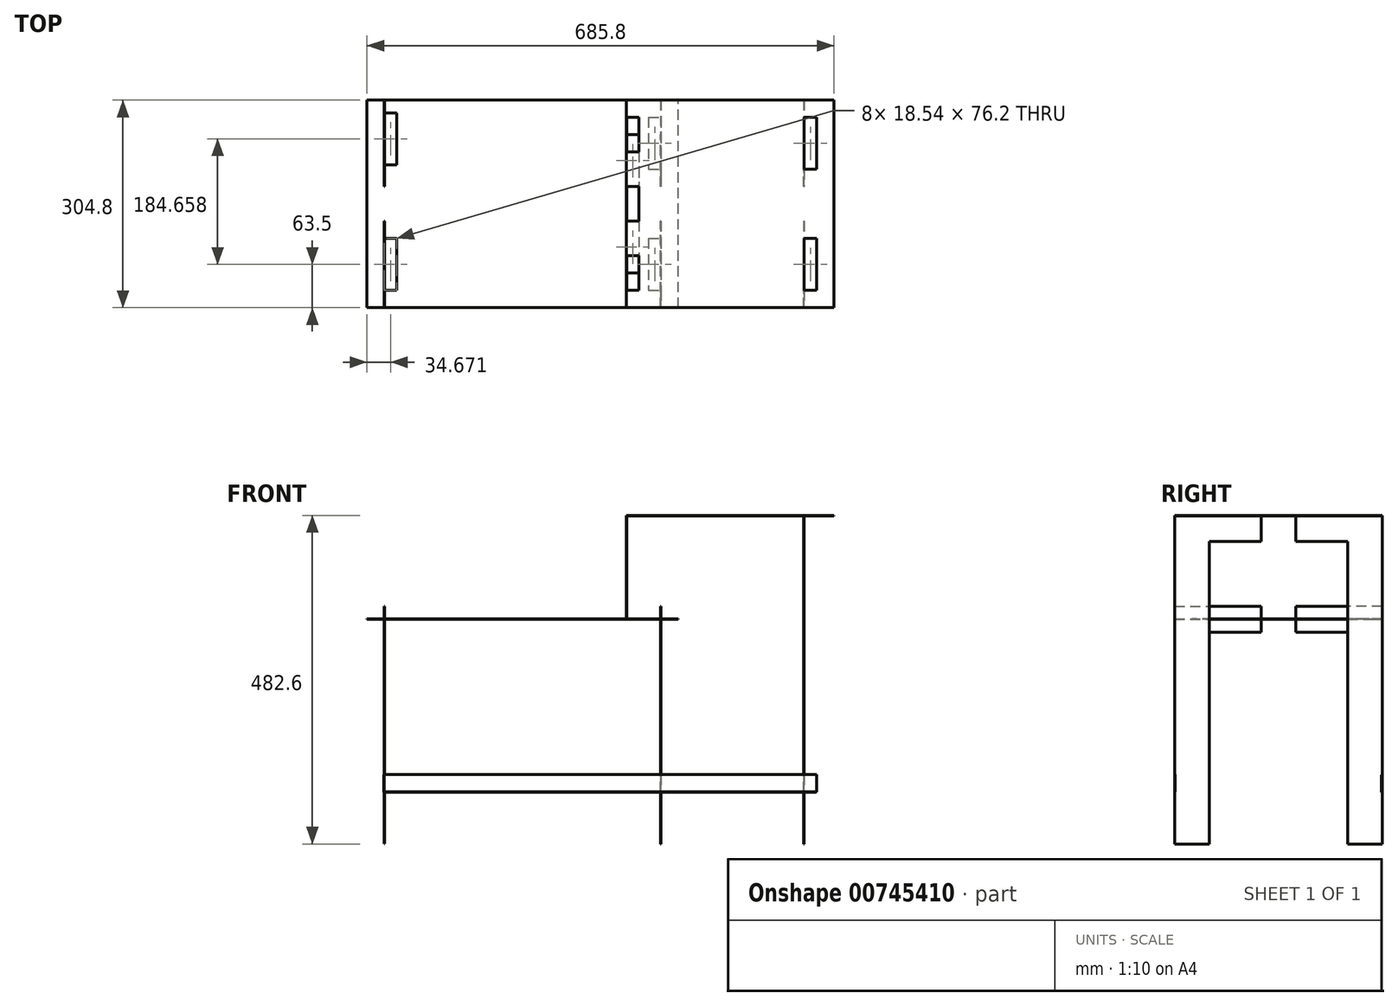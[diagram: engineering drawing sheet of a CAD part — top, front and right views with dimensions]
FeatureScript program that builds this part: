
annotation { "Feature Type Name" : "Feature", "Feature Type Description" : "" }
export const myFeature = defineFeature(function(context is Context, id is Id, definition is map)
    precondition{}
    {
        {
            assignVariable(context, id + "F0", {"name" : "ply", "anyValue" : .73});
        }
        {
            var Q0;
            Q0=qCreatedBy(makeId("Top.planeOp"),FACE);
            var sketch = newSketch(context, id + "F1", { "sketchPlane" : qUnion([Q0])});
            skLineSegment(sketch, "E0.bottom", {"start": v(0, 0) * mm, "end": v(-457.2, 0) * mm});
            skLineSegment(sketch, "E0.top", {"start": v(0, 304.8) * mm, "end": v(-457.2, 304.8) * mm});
            skLineSegment(sketch, "E0.left", {"start": v(0, 0) * mm, "end": v(0, 304.8) * mm});
            skLineSegment(sketch, "E0.right", {"start": v(-457.2, 0) * mm, "end": v(-457.2, 304.8) * mm});
            skLineSegment(sketch, "E1.bottom", {"start": v(-76.2, 254) * mm, "end": v(-57.66, 254) * mm});
            skLineSegment(sketch, "E1.top", {"start": v(-76.2, 177.8) * mm, "end": v(-57.66, 177.8) * mm});
            skLineSegment(sketch, "E1.left", {"start": v(-76.2, 254) * mm, "end": v(-76.2, 177.8) * mm});
            skLineSegment(sketch, "E1.right", {"start": v(-57.66, 254) * mm, "end": v(-57.66, 177.8) * mm});
            skLineSegment(sketch, "E2.bottom", {"start": v(-76.2, 127) * mm, "end": v(-57.66, 127) * mm});
            skLineSegment(sketch, "E2.top", {"start": v(-76.2, 50.8) * mm, "end": v(-57.66, 50.8) * mm});
            skLineSegment(sketch, "E2.left", {"start": v(-76.2, 127) * mm, "end": v(-76.2, 50.8) * mm});
            skLineSegment(sketch, "E2.right", {"start": v(-57.66, 127) * mm, "end": v(-57.66, 50.8) * mm});
            skLineSegment(sketch, "E3.bottom", {"start": v(-43.94, 279.4) * mm, "end": v(-25.4, 279.4) * mm});
            skLineSegment(sketch, "E3.top", {"start": v(-43.94, 203.2) * mm, "end": v(-25.4, 203.2) * mm});
            skLineSegment(sketch, "E3.left", {"start": v(-43.94, 279.4) * mm, "end": v(-43.94, 203.2) * mm});
            skLineSegment(sketch, "E3.right", {"start": v(-25.4, 279.4) * mm, "end": v(-25.4, 203.2) * mm});
            skLineSegment(sketch, "E4.bottom", {"start": v(-43.94, 101.6) * mm, "end": v(-25.4, 101.6) * mm});
            skLineSegment(sketch, "E4.top", {"start": v(-43.94, 25.4) * mm, "end": v(-25.4, 25.4) * mm});
            skLineSegment(sketch, "E4.left", {"start": v(-43.94, 101.6) * mm, "end": v(-43.94, 25.4) * mm});
            skLineSegment(sketch, "E4.right", {"start": v(-25.4, 101.6) * mm, "end": v(-25.4, 25.4) * mm});
            skLineSegment(sketch, "E5.bottom", {"start": v(-431.8, 101.6) * mm, "end": v(-413.26, 101.6) * mm});
            skLineSegment(sketch, "E5.top", {"start": v(-431.8, 25.4) * mm, "end": v(-413.26, 25.4) * mm});
            skLineSegment(sketch, "E5.left", {"start": v(-431.8, 101.6) * mm, "end": v(-431.8, 25.4) * mm});
            skLineSegment(sketch, "E5.right", {"start": v(-413.26, 101.6) * mm, "end": v(-413.26, 25.4) * mm});
            skLineSegment(sketch, "E6.bottom", {"start": v(-431.8, 286.26) * mm, "end": v(-413.26, 286.26) * mm});
            skLineSegment(sketch, "E6.top", {"start": v(-431.8, 210.06) * mm, "end": v(-413.26, 210.06) * mm});
            skLineSegment(sketch, "E6.left", {"start": v(-431.8, 286.26) * mm, "end": v(-431.8, 210.06) * mm});
            skLineSegment(sketch, "E6.right", {"start": v(-413.26, 286.26) * mm, "end": v(-413.26, 210.06) * mm});
            skSolve(sketch);
        }
        {
            var Q0;
            Q0=makeQuery(id+"F1.imprint","IMPRINT",FACE,{"disambiguationData":[TD([[makeQuery(id+"F1.imprint","IMPRINT",EDGE,{"derivedFrom":sQuery(id+"F1.wireOp",EDGE,"E0.bottom")}),-1.0]])]});
            var Q1;
            Q1 = qSketchRegion(id + "FDRdPOymtDaT9Mf_1", true);
            extrude(context, id + "F2", {"entities" : qUnion([Q0, Q1]), "depth" : (getVariable(context, 'ply')) * mm, "offsetDistance" : 25.4 * mm});
        }
        {
            var Q0;
            Q0=qCreatedBy(makeId("Top.planeOp"),FACE);
            cPlane(context, id + "F3", {"entities" : qUnion([Q0]), "cplaneType" : CPlaneType.OFFSET, "offset" : 152.4 * mm, "width" : 152.4 * mm, "height" : 152.4 * mm});
        }
        {
            var Q0;
            Q0=qCreatedBy(id+"F3.planeOp",FACE);
            var sketch = newSketch(context, id + "F4", { "sketchPlane" : qUnion([Q0])});
            skLineSegment(sketch, "E7.bottom", {"start": v(-76.2, 0) * mm, "end": v(228.6, 0) * mm});
            skLineSegment(sketch, "E7.top", {"start": v(-76.2, 304.8) * mm, "end": v(228.6, 304.8) * mm});
            skLineSegment(sketch, "E7.left", {"start": v(-76.2, 0) * mm, "end": v(-76.2, 25.4) * mm});
            skLineSegment(sketch, "E7.right", {"start": v(228.6, 0) * mm, "end": v(228.6, 304.8) * mm});
            skLineSegment(sketch, "E8.bottom", {"start": v(-76.2, 228.6) * mm, "end": v(-57.66, 228.6) * mm});
            skLineSegment(sketch, "E8.top", {"start": v(-76.2, 279.4) * mm, "end": v(-57.66, 279.4) * mm});
            skLineSegment(sketch, "E8.right", {"start": v(-57.66, 228.6) * mm, "end": v(-57.66, 279.4) * mm});
            skLineSegment(sketch, "E9.bottom", {"start": v(-76.2, 177.8) * mm, "end": v(-57.66, 177.8) * mm});
            skLineSegment(sketch, "E9.top", {"start": v(-76.2, 127) * mm, "end": v(-57.66, 127) * mm});
            skLineSegment(sketch, "E9.right", {"start": v(-57.66, 177.8) * mm, "end": v(-57.66, 127) * mm});
            skLineSegment(sketch, "E10.bottom", {"start": v(-76.2, 76.2) * mm, "end": v(-57.66, 76.2) * mm});
            skLineSegment(sketch, "E10.top", {"start": v(-76.2, 25.4) * mm, "end": v(-57.66, 25.4) * mm});
            skLineSegment(sketch, "E10.right", {"start": v(-57.66, 76.2) * mm, "end": v(-57.66, 25.4) * mm});
            skLineSegment(sketch, "E11.trimOffspring", {"start": v(-76.2, 279.4) * mm, "end": v(-76.2, 304.8) * mm});
            skLineSegment(sketch, "E12.trimOffspring", {"start": v(-76.2, 177.8) * mm, "end": v(-76.2, 228.6) * mm});
            skLineSegment(sketch, "E13.trimOffspring", {"start": v(-76.2, 76.2) * mm, "end": v(-76.2, 127) * mm});
            skLineSegment(sketch, "E14.bottom", {"start": v(203.2, 25.4) * mm, "end": v(184.66, 25.4) * mm});
            skLineSegment(sketch, "E14.top", {"start": v(203.2, 101.6) * mm, "end": v(184.66, 101.6) * mm});
            skLineSegment(sketch, "E14.left", {"start": v(203.2, 25.4) * mm, "end": v(203.2, 101.6) * mm});
            skLineSegment(sketch, "E14.right", {"start": v(184.66, 25.4) * mm, "end": v(184.66, 101.6) * mm});
            skLineSegment(sketch, "E15.bottom", {"start": v(184.66, 203.2) * mm, "end": v(203.2, 203.2) * mm});
            skLineSegment(sketch, "E15.top", {"start": v(184.66, 279.4) * mm, "end": v(203.2, 279.4) * mm});
            skLineSegment(sketch, "E15.left", {"start": v(184.66, 203.2) * mm, "end": v(184.66, 279.4) * mm});
            skLineSegment(sketch, "E15.right", {"start": v(203.2, 203.2) * mm, "end": v(203.2, 279.4) * mm});
            skSolve(sketch);
        }
        {
            var Q0;
            Q0 = qSketchRegion(id + "F4", true);
            extrude(context, id + "F5", {"entities" : qUnion([Q0]), "oppositeDirection" : true, "depth" : (getVariable(context, 'ply')) * mm, "offsetDistance" : 25.4 * mm});
        }
        {
            var Q0;
            Q0=makeQuery(id+"F5.opExtrude","SWEPT_FACE",FACE,{"disambiguationData":[OSD([sQuery(id+"F4.wireOp",EDGE,"E11.trimOffspring")])]});
            var sketch = newSketch(context, id + "F6", { "sketchPlane" : qUnion([Q0])});
            skLineSegment(sketch, "E16.bottom", {"start": v(-304.8, 152.4) * mm, "end": v(0, 152.4) * mm});
            skLineSegment(sketch, "E16.top", {"start": v(-304.8, 0) * mm, "end": v(0, 0) * mm});
            skLineSegment(sketch, "E16.left", {"start": v(-304.8, 152.4) * mm, "end": v(-304.8, 0) * mm});
            skLineSegment(sketch, "E16.right", {"start": v(0, 152.4) * mm, "end": v(0, 0) * mm});
            skSolve(sketch);
        }
        {
            var Q0;
            Q0 = qSketchRegion(id + "F6", true);
            extrude(context, id + "F7", {"entities" : qUnion([Q0]), "oppositeDirection" : true, "depth" : (getVariable(context, 'ply')) * mm, "offsetDistance" : 25.4 * mm});
        }
        {
            var Q0;
            Q0=makeQuery(id+"F5.opExtrude","SWEPT_BODY",BODY,{"disambiguationData":[OSD([sQuery(id+"F4.wireOp",EDGE,"E7.bottom"),sQuery(id+"F4.wireOp",EDGE,"E7.top"),sQuery(id+"F4.wireOp",EDGE,"E7.left"),sQuery(id+"F4.wireOp",EDGE,"E7.right"),sQuery(id+"F4.wireOp",EDGE,"E8.bottom"),sQuery(id+"F4.wireOp",EDGE,"E8.top"),sQuery(id+"F4.wireOp",EDGE,"E8.right"),sQuery(id+"F4.wireOp",EDGE,"E9.bottom"),sQuery(id+"F4.wireOp",EDGE,"E9.top"),sQuery(id+"F4.wireOp",EDGE,"E9.right"),sQuery(id+"F4.wireOp",EDGE,"E10.bottom"),sQuery(id+"F4.wireOp",EDGE,"E10.top"),sQuery(id+"F4.wireOp",EDGE,"E10.right"),sQuery(id+"F4.wireOp",EDGE,"E11.trimOffspring"),sQuery(id+"F4.wireOp",EDGE,"E12.trimOffspring"),sQuery(id+"F4.wireOp",EDGE,"E13.trimOffspring")])]});
            var Q1;
            Q1=makeQuery(id+"F7.opExtrude","SWEPT_BODY",BODY,{"disambiguationData":[OSD([sQuery(id+"F6.wireOp",EDGE,"E16.bottom"),sQuery(id+"F6.wireOp",EDGE,"E16.top"),sQuery(id+"F6.wireOp",EDGE,"E16.left"),sQuery(id+"F6.wireOp",EDGE,"E16.right")])]});
            booleanBodies(context, id + "F8", {"operationType" : BooleanOperationType.SUBTRACTION, "tools" : qUnion([Q0]), "targets" : qUnion([Q1]), "keepTools" : true});
        }
        {
            var Q0;
            Q0=makeQuery(id+"F5.opExtrude","SWEPT_FACE",FACE,{"disambiguationData":[OSD([sQuery(id+"F4.wireOp",EDGE,"E7.top")])]});
            cPlane(context, id + "F9", {"entities" : qUnion([Q0]), "cplaneType" : CPlaneType.OFFSET, "offset" : 152.4 * mm, "oppositeDirection" : true, "width" : 152.4 * mm, "height" : 152.4 * mm});
        }
        {
            var Q0;
            Q0=qCreatedBy(makeId("Right.planeOp"),FACE);
            var sketch = newSketch(context, id + "F10", { "sketchPlane" : qUnion([Q0])});
            skLineSegment(sketch, "E17.bottom", {"start": v(0, 152.4) * mm, "end": v(127, 152.4) * mm});
            skLineSegment(sketch, "E17.top", {"start": v(0, -330.2) * mm, "end": v(50.8, -330.2) * mm});
            skLineSegment(sketch, "E17.left", {"start": v(0, 152.4) * mm, "end": v(0, -330.2) * mm});
            skLineSegment(sketch, "E17.right", {"start": v(127, 152.4) * mm, "end": v(127, 114.3) * mm});
            skLineSegment(sketch, "E18.top", {"start": v(127, 114.3) * mm, "end": v(50.8, 114.3) * mm});
            skLineSegment(sketch, "E18.right", {"start": v(50.8, -330.2) * mm, "end": v(50.8, 114.3) * mm});
            skLineSegment(sketch, "E19.MirrorCS", {"start": v(254, -330.2) * mm, "end": v(254, 114.3) * mm});
            skLineSegment(sketch, "E20.MirrorCS", {"start": v(177.8, 114.3) * mm, "end": v(254, 114.3) * mm});
            skLineSegment(sketch, "E21.MirrorCS", {"start": v(177.8, 152.4) * mm, "end": v(177.8, 114.3) * mm});
            skLineSegment(sketch, "E22.MirrorCS", {"start": v(304.8, 152.4) * mm, "end": v(304.8, -330.2) * mm});
            skLineSegment(sketch, "E23.MirrorCS", {"start": v(304.8, 152.4) * mm, "end": v(177.8, 152.4) * mm});
            skLineSegment(sketch, "E24.MirrorCS", {"start": v(304.8, -330.2) * mm, "end": v(254, -330.2) * mm});
            skSolve(sketch);
        }
        {
            var Q0;
            Q0 = qSketchRegion(id + "F10", true);
            extrude(context, id + "F11", {"entities" : qUnion([Q0]), "depth" : (getVariable(context, 'ply')) * mm, "offsetDistance" : 25.4 * mm});
        }
        {
            var Q0;
            Q0=makeQuery(id+"F11.opExtrude","SWEPT_BODY",BODY,{"disambiguationData":[OSD([sQuery(id+"F10.wireOp",EDGE,"E17.bottom"),sQuery(id+"F10.wireOp",EDGE,"E17.top"),sQuery(id+"F10.wireOp",EDGE,"E17.left"),sQuery(id+"F10.wireOp",EDGE,"E17.right"),sQuery(id+"F10.wireOp",EDGE,"E18.top"),sQuery(id+"F10.wireOp",EDGE,"E18.right")])]});
            var Q1;
            Q1=makeQuery(id+"F5.opExtrude","SWEPT_FACE",FACE,{"disambiguationData":[OSD([sQuery(id+"F4.wireOp",EDGE,"E14.right")])]});
            transform(context, id + "F12", {"entities" : qUnion([Q0]), "transformType" : TransformType.TRANSLATION_DISTANCE, "transformDirection" : qUnion([Q1]), "distance" : 184.15 * mm, "makeCopy" : false});
        }
        {
            var Q0;
            Q0=makeQuery(id+"F5.opExtrude","SWEPT_BODY",BODY,{"disambiguationData":[OSD([sQuery(id+"F4.wireOp",EDGE,"E7.bottom"),sQuery(id+"F4.wireOp",EDGE,"E7.top"),sQuery(id+"F4.wireOp",EDGE,"E7.left"),sQuery(id+"F4.wireOp",EDGE,"E7.right"),sQuery(id+"F4.wireOp",EDGE,"E8.bottom"),sQuery(id+"F4.wireOp",EDGE,"E8.top"),sQuery(id+"F4.wireOp",EDGE,"E8.right"),sQuery(id+"F4.wireOp",EDGE,"E9.bottom"),sQuery(id+"F4.wireOp",EDGE,"E9.top"),sQuery(id+"F4.wireOp",EDGE,"E9.right"),sQuery(id+"F4.wireOp",EDGE,"E10.bottom"),sQuery(id+"F4.wireOp",EDGE,"E10.top"),sQuery(id+"F4.wireOp",EDGE,"E10.right"),sQuery(id+"F4.wireOp",EDGE,"E11.trimOffspring"),sQuery(id+"F4.wireOp",EDGE,"E12.trimOffspring"),sQuery(id+"F4.wireOp",EDGE,"E13.trimOffspring"),sQuery(id+"F4.wireOp",EDGE,"E14.bottom"),sQuery(id+"F4.wireOp",EDGE,"E14.top"),sQuery(id+"F4.wireOp",EDGE,"E14.left"),sQuery(id+"F4.wireOp",EDGE,"E14.right"),sQuery(id+"F4.wireOp",EDGE,"E15.bottom"),sQuery(id+"F4.wireOp",EDGE,"E15.top"),sQuery(id+"F4.wireOp",EDGE,"E15.left"),sQuery(id+"F4.wireOp",EDGE,"E15.right")])]});
            var Q1;
            Q1=makeQuery(id+"F11.opExtrude","SWEPT_BODY",BODY,{"disambiguationData":[OSD([sQuery(id+"F10.wireOp",EDGE,"E17.bottom"),sQuery(id+"F10.wireOp",EDGE,"E17.top"),sQuery(id+"F10.wireOp",EDGE,"E17.left"),sQuery(id+"F10.wireOp",EDGE,"E17.right"),sQuery(id+"F10.wireOp",EDGE,"E18.top"),sQuery(id+"F10.wireOp",EDGE,"E18.right")])]});
            booleanBodies(context, id + "F13", {"operationType" : BooleanOperationType.SUBTRACTION, "tools" : qUnion([Q0]), "targets" : qUnion([Q1]), "keepTools" : true});
        }
        {
            var Q0;
            Q0=makeQuery(id+"F11.opExtrude","SWEPT_BODY",BODY,{"disambiguationData":[OSD([sQuery(id+"F10.wireOp",EDGE,"E19.MirrorCS"),sQuery(id+"F10.wireOp",EDGE,"E20.MirrorCS"),sQuery(id+"F10.wireOp",EDGE,"E21.MirrorCS"),sQuery(id+"F10.wireOp",EDGE,"E22.MirrorCS"),sQuery(id+"F10.wireOp",EDGE,"E23.MirrorCS"),sQuery(id+"F10.wireOp",EDGE,"E24.MirrorCS")])]});
            var Q1;
            Q1=makeQuery(id+"F5.opExtrude","SWEPT_FACE",FACE,{"disambiguationData":[OSD([sQuery(id+"F4.wireOp",EDGE,"E15.left")])]});
            transform(context, id + "F14", {"entities" : qUnion([Q0]), "transformType" : TransformType.TRANSLATION_DISTANCE, "transformDirection" : qUnion([Q1]), "distance" : 184.15 * mm, "makeCopy" : false});
        }
        {
            var Q0;
            Q0=makeQuery(id+"F5.opExtrude","SWEPT_BODY",BODY,{"disambiguationData":[OSD([sQuery(id+"F4.wireOp",EDGE,"E7.bottom"),sQuery(id+"F4.wireOp",EDGE,"E7.top"),sQuery(id+"F4.wireOp",EDGE,"E7.left"),sQuery(id+"F4.wireOp",EDGE,"E7.right"),sQuery(id+"F4.wireOp",EDGE,"E8.bottom"),sQuery(id+"F4.wireOp",EDGE,"E8.top"),sQuery(id+"F4.wireOp",EDGE,"E8.right"),sQuery(id+"F4.wireOp",EDGE,"E9.bottom"),sQuery(id+"F4.wireOp",EDGE,"E9.top"),sQuery(id+"F4.wireOp",EDGE,"E9.right"),sQuery(id+"F4.wireOp",EDGE,"E10.bottom"),sQuery(id+"F4.wireOp",EDGE,"E10.top"),sQuery(id+"F4.wireOp",EDGE,"E10.right"),sQuery(id+"F4.wireOp",EDGE,"E11.trimOffspring"),sQuery(id+"F4.wireOp",EDGE,"E12.trimOffspring"),sQuery(id+"F4.wireOp",EDGE,"E13.trimOffspring"),sQuery(id+"F4.wireOp",EDGE,"E14.bottom"),sQuery(id+"F4.wireOp",EDGE,"E14.top"),sQuery(id+"F4.wireOp",EDGE,"E14.left"),sQuery(id+"F4.wireOp",EDGE,"E14.right"),sQuery(id+"F4.wireOp",EDGE,"E15.bottom"),sQuery(id+"F4.wireOp",EDGE,"E15.top"),sQuery(id+"F4.wireOp",EDGE,"E15.left"),sQuery(id+"F4.wireOp",EDGE,"E15.right")])]});
            var Q1;
            Q1=makeQuery(id+"F11.opExtrude","SWEPT_BODY",BODY,{"disambiguationData":[OSD([sQuery(id+"F10.wireOp",EDGE,"E19.MirrorCS"),sQuery(id+"F10.wireOp",EDGE,"E20.MirrorCS"),sQuery(id+"F10.wireOp",EDGE,"E21.MirrorCS"),sQuery(id+"F10.wireOp",EDGE,"E22.MirrorCS"),sQuery(id+"F10.wireOp",EDGE,"E23.MirrorCS"),sQuery(id+"F10.wireOp",EDGE,"E24.MirrorCS")])]});
            booleanBodies(context, id + "F15", {"operationType" : BooleanOperationType.SUBTRACTION, "tools" : qUnion([Q0]), "targets" : qUnion([Q1]), "keepTools" : true});
        }
        {
            var Q0;
            Q0=makeQuery(id+"F2.opExtrude","SWEPT_BODY",BODY,{"disambiguationData":[OSD([sQuery(id+"F1.wireOp",EDGE,"E0.bottom"),sQuery(id+"F1.wireOp",EDGE,"E0.top"),sQuery(id+"F1.wireOp",EDGE,"E0.left"),sQuery(id+"F1.wireOp",EDGE,"E0.right"),sQuery(id+"F1.wireOp",EDGE,"E1.bottom"),sQuery(id+"F1.wireOp",EDGE,"E1.top"),sQuery(id+"F1.wireOp",EDGE,"E1.left"),sQuery(id+"F1.wireOp",EDGE,"E1.right"),sQuery(id+"F1.wireOp",EDGE,"E2.bottom"),sQuery(id+"F1.wireOp",EDGE,"E2.top"),sQuery(id+"F1.wireOp",EDGE,"E2.left"),sQuery(id+"F1.wireOp",EDGE,"E2.right")])]});
            var Q1;
            Q1=makeQuery(id+"F7.opExtrude","SWEPT_BODY",BODY,{"disambiguationData":[OSD([sQuery(id+"F6.wireOp",EDGE,"E16.bottom"),sQuery(id+"F6.wireOp",EDGE,"E16.top"),sQuery(id+"F6.wireOp",EDGE,"E16.left"),sQuery(id+"F6.wireOp",EDGE,"E16.right")])]});
            booleanBodies(context, id + "F16", {"operationType" : BooleanOperationType.SUBTRACTION, "tools" : qUnion([Q0]), "targets" : qUnion([Q1]), "keepTools" : true});
        }
        {
            var Q0;
            Q0=qCreatedBy(makeId("Right.planeOp"),FACE);
            var sketch = newSketch(context, id + "F17", { "sketchPlane" : qUnion([Q0])});
            skLineSegment(sketch, "E25.bottom", {"start": v(0, 18.54) * mm, "end": v(127, 18.54) * mm});
            skLineSegment(sketch, "E25.top", {"start": v(0, -330.2) * mm, "end": v(50.8, -330.2) * mm});
            skLineSegment(sketch, "E25.left", {"start": v(0, 18.54) * mm, "end": v(0, -330.2) * mm});
            skLineSegment(sketch, "E25.right", {"start": v(127, 18.54) * mm, "end": v(127, -19.56) * mm});
            skLineSegment(sketch, "E26.top", {"start": v(127, -19.56) * mm, "end": v(50.8, -19.56) * mm});
            skLineSegment(sketch, "E26.right", {"start": v(50.8, -330.2) * mm, "end": v(50.8, -19.56) * mm});
            skLineSegment(sketch, "E27.MirrorCS", {"start": v(177.8, 18.54) * mm, "end": v(177.8, -19.56) * mm});
            skLineSegment(sketch, "E28.MirrorCS", {"start": v(254, -330.2) * mm, "end": v(254, -19.56) * mm});
            skLineSegment(sketch, "E29.MirrorCS", {"start": v(177.8, -19.56) * mm, "end": v(254, -19.56) * mm});
            skLineSegment(sketch, "E30.MirrorCS", {"start": v(304.8, 18.54) * mm, "end": v(304.8, -330.2) * mm});
            skLineSegment(sketch, "E31.MirrorCS", {"start": v(304.8, -330.2) * mm, "end": v(254, -330.2) * mm});
            skLineSegment(sketch, "E32.MirrorCS", {"start": v(304.8, 18.54) * mm, "end": v(177.8, 18.54) * mm});
            skSolve(sketch);
        }
        {
            var Q0;
            Q0 = qSketchRegion(id + "F17", true);
            extrude(context, id + "F18", {"entities" : qUnion([Q0]), "oppositeDirection" : true, "depth" : (getVariable(context, 'ply')) * mm, "offsetDistance" : 25.4 * mm});
        }
        {
            var Q0;
            Q0=makeQuery(id+"F18.opExtrude","SWEPT_BODY",BODY,{"disambiguationData":[OSD([sQuery(id+"F17.wireOp",EDGE,"E25.bottom"),sQuery(id+"F17.wireOp",EDGE,"E25.top"),sQuery(id+"F17.wireOp",EDGE,"E25.left"),sQuery(id+"F17.wireOp",EDGE,"E25.right"),sQuery(id+"F17.wireOp",EDGE,"E26.top"),sQuery(id+"F17.wireOp",EDGE,"E26.right")])]});
            var Q1;
            Q1=makeQuery(id+"F2.opExtrude","SWEPT_FACE",FACE,{"disambiguationData":[OSD([sQuery(id+"F1.wireOp",EDGE,"E0.right")])]});
            transform(context, id + "F19", {"entities" : qUnion([Q0]), "transformType" : TransformType.TRANSLATION_DISTANCE, "transformDirection" : qUnion([Q1]), "distance" : 25.4 * mm, "makeCopy" : false});
        }
        {
            var Q0;
            Q0=makeQuery(id+"F2.opExtrude","SWEPT_BODY",BODY,{"disambiguationData":[OSD([sQuery(id+"F1.wireOp",EDGE,"E0.bottom"),sQuery(id+"F1.wireOp",EDGE,"E0.top"),sQuery(id+"F1.wireOp",EDGE,"E0.left"),sQuery(id+"F1.wireOp",EDGE,"E0.right"),sQuery(id+"F1.wireOp",EDGE,"E1.bottom"),sQuery(id+"F1.wireOp",EDGE,"E1.top"),sQuery(id+"F1.wireOp",EDGE,"E1.left"),sQuery(id+"F1.wireOp",EDGE,"E1.right"),sQuery(id+"F1.wireOp",EDGE,"E2.bottom"),sQuery(id+"F1.wireOp",EDGE,"E2.top"),sQuery(id+"F1.wireOp",EDGE,"E2.left"),sQuery(id+"F1.wireOp",EDGE,"E2.right"),sQuery(id+"F1.wireOp",EDGE,"E3.bottom"),sQuery(id+"F1.wireOp",EDGE,"E3.top"),sQuery(id+"F1.wireOp",EDGE,"E3.left"),sQuery(id+"F1.wireOp",EDGE,"E3.right"),sQuery(id+"F1.wireOp",EDGE,"E4.bottom"),sQuery(id+"F1.wireOp",EDGE,"E4.top"),sQuery(id+"F1.wireOp",EDGE,"E4.left"),sQuery(id+"F1.wireOp",EDGE,"E4.right")])]});
            var Q1;
            Q1=makeQuery(id+"F18.opExtrude","SWEPT_BODY",BODY,{"disambiguationData":[OSD([sQuery(id+"F17.wireOp",EDGE,"E25.bottom"),sQuery(id+"F17.wireOp",EDGE,"E25.top"),sQuery(id+"F17.wireOp",EDGE,"E25.left"),sQuery(id+"F17.wireOp",EDGE,"E25.right"),sQuery(id+"F17.wireOp",EDGE,"E26.top"),sQuery(id+"F17.wireOp",EDGE,"E26.right")])]});
            booleanBodies(context, id + "F20", {"operationType" : BooleanOperationType.SUBTRACTION, "tools" : qUnion([Q0]), "targets" : qUnion([Q1]), "keepTools" : true});
        }
        {
            var Q0;
            Q0=makeQuery(id+"F18.opExtrude","SWEPT_BODY",BODY,{"disambiguationData":[OSD([sQuery(id+"F17.wireOp",EDGE,"E27.MirrorCS"),sQuery(id+"F17.wireOp",EDGE,"E28.MirrorCS"),sQuery(id+"F17.wireOp",EDGE,"E29.MirrorCS"),sQuery(id+"F17.wireOp",EDGE,"E30.MirrorCS"),sQuery(id+"F17.wireOp",EDGE,"E31.MirrorCS"),sQuery(id+"F17.wireOp",EDGE,"E32.MirrorCS")])]});
            var Q1;
            Q1=makeQuery(id+"F2.opExtrude","SWEPT_FACE",FACE,{"disambiguationData":[OSD([sQuery(id+"F1.wireOp",EDGE,"E0.right")])]});
            transform(context, id + "F21", {"entities" : qUnion([Q0]), "transformType" : TransformType.TRANSLATION_DISTANCE, "transformDirection" : qUnion([Q1]), "distance" : 25.4 * mm, "makeCopy" : false});
        }
        {
            var Q0;
            Q0=makeQuery(id+"F2.opExtrude","SWEPT_BODY",BODY,{"disambiguationData":[OSD([sQuery(id+"F1.wireOp",EDGE,"E0.bottom"),sQuery(id+"F1.wireOp",EDGE,"E0.top"),sQuery(id+"F1.wireOp",EDGE,"E0.left"),sQuery(id+"F1.wireOp",EDGE,"E0.right"),sQuery(id+"F1.wireOp",EDGE,"E1.bottom"),sQuery(id+"F1.wireOp",EDGE,"E1.top"),sQuery(id+"F1.wireOp",EDGE,"E1.left"),sQuery(id+"F1.wireOp",EDGE,"E1.right"),sQuery(id+"F1.wireOp",EDGE,"E2.bottom"),sQuery(id+"F1.wireOp",EDGE,"E2.top"),sQuery(id+"F1.wireOp",EDGE,"E2.left"),sQuery(id+"F1.wireOp",EDGE,"E2.right"),sQuery(id+"F1.wireOp",EDGE,"E3.bottom"),sQuery(id+"F1.wireOp",EDGE,"E3.top"),sQuery(id+"F1.wireOp",EDGE,"E3.left"),sQuery(id+"F1.wireOp",EDGE,"E3.right"),sQuery(id+"F1.wireOp",EDGE,"E4.bottom"),sQuery(id+"F1.wireOp",EDGE,"E4.top"),sQuery(id+"F1.wireOp",EDGE,"E4.left"),sQuery(id+"F1.wireOp",EDGE,"E4.right")])]});
            var Q1;
            Q1=makeQuery(id+"F18.opExtrude","SWEPT_BODY",BODY,{"disambiguationData":[OSD([sQuery(id+"F17.wireOp",EDGE,"E27.MirrorCS"),sQuery(id+"F17.wireOp",EDGE,"E28.MirrorCS"),sQuery(id+"F17.wireOp",EDGE,"E29.MirrorCS"),sQuery(id+"F17.wireOp",EDGE,"E30.MirrorCS"),sQuery(id+"F17.wireOp",EDGE,"E31.MirrorCS"),sQuery(id+"F17.wireOp",EDGE,"E32.MirrorCS")])]});
            booleanBodies(context, id + "F22", {"operationType" : BooleanOperationType.SUBTRACTION, "tools" : qUnion([Q0]), "targets" : qUnion([Q1]), "keepTools" : true});
        }
        {
            var Q0;
            Q0=makeQuery(id+"F2.opExtrude","SWEPT_FACE",FACE,{"disambiguationData":[OSD([sQuery(id+"F1.wireOp",EDGE,"E0.right")])]});
            var sketch = newSketch(context, id + "F23", { "sketchPlane" : qUnion([Q0])});
            skLineSegment(sketch, "E33.bottom", {"start": v(-304.8, 18.54) * mm, "end": v(-177.8, 18.54) * mm});
            skLineSegment(sketch, "E33.top", {"start": v(-304.8, -329.95) * mm, "end": v(-254, -329.95) * mm});
            skLineSegment(sketch, "E33.left", {"start": v(-304.8, 18.54) * mm, "end": v(-304.8, -329.95) * mm});
            skLineSegment(sketch, "E33.right", {"start": v(-177.8, 18.54) * mm, "end": v(-177.8, -18.8) * mm});
            skLineSegment(sketch, "E34.top", {"start": v(-177.8, -18.8) * mm, "end": v(-254, -18.8) * mm});
            skLineSegment(sketch, "E34.right", {"start": v(-254, -329.95) * mm, "end": v(-254, -18.8) * mm});
            skLineSegment(sketch, "E35.MirrorCS", {"start": v(-50.8, -329.95) * mm, "end": v(-50.8, -18.8) * mm});
            skLineSegment(sketch, "E36.MirrorCS", {"start": v(-127, -18.8) * mm, "end": v(-50.8, -18.8) * mm});
            skLineSegment(sketch, "E37.MirrorCS", {"start": v(-127, 18.54) * mm, "end": v(-127, -18.8) * mm});
            skLineSegment(sketch, "E38.MirrorCS", {"start": v(0, 18.54) * mm, "end": v(0, -329.95) * mm});
            skLineSegment(sketch, "E39.MirrorCS", {"start": v(0, -329.95) * mm, "end": v(-50.8, -329.95) * mm});
            skLineSegment(sketch, "E40.MirrorCS", {"start": v(0, 18.54) * mm, "end": v(-127, 18.54) * mm});
            skSolve(sketch);
        }
        {
            var Q0;
            Q0 = qSketchRegion(id + "F23", true);
            extrude(context, id + "F24", {"entities" : qUnion([Q0]), "oppositeDirection" : true, "depth" : (getVariable(context, 'ply')) * mm, "offsetDistance" : 25.4 * mm});
        }
        {
            var Q0;
            Q0=makeQuery(id+"F24.opExtrude","SWEPT_BODY",BODY,{"disambiguationData":[OSD([sQuery(id+"F23.wireOp",EDGE,"E33.bottom"),sQuery(id+"F23.wireOp",EDGE,"E33.top"),sQuery(id+"F23.wireOp",EDGE,"E33.left"),sQuery(id+"F23.wireOp",EDGE,"E33.right"),sQuery(id+"F23.wireOp",EDGE,"E34.top"),sQuery(id+"F23.wireOp",EDGE,"E34.right")])]});
            var Q1;
            Q1=makeQuery(id+"F24.opExtrude","SWEPT_BODY",BODY,{"disambiguationData":[OSD([sQuery(id+"F23.wireOp",EDGE,"E35.MirrorCS"),sQuery(id+"F23.wireOp",EDGE,"E36.MirrorCS"),sQuery(id+"F23.wireOp",EDGE,"E37.MirrorCS"),sQuery(id+"F23.wireOp",EDGE,"E38.MirrorCS"),sQuery(id+"F23.wireOp",EDGE,"E39.MirrorCS"),sQuery(id+"F23.wireOp",EDGE,"E40.MirrorCS")])]});
            var Q2;
            Q2=makeQuery(id+"F2.opExtrude","SWEPT_FACE",FACE,{"disambiguationData":[OSD([sQuery(id+"F1.wireOp",EDGE,"E0.right")])]});
            transform(context, id + "F25", {"entities" : qUnion([Q0, Q1]), "transformType" : TransformType.TRANSLATION_DISTANCE, "transformDirection" : qUnion([Q2]), "distance" : 25.4 * mm, "oppositeDirection" : true, "makeCopy" : false});
        }
        {
            var Q0;
            Q0=makeQuery(id+"F2.opExtrude","SWEPT_BODY",BODY,{"disambiguationData":[OSD([sQuery(id+"F1.wireOp",EDGE,"E0.bottom"),sQuery(id+"F1.wireOp",EDGE,"E0.top"),sQuery(id+"F1.wireOp",EDGE,"E0.left"),sQuery(id+"F1.wireOp",EDGE,"E0.right"),sQuery(id+"F1.wireOp",EDGE,"E1.bottom"),sQuery(id+"F1.wireOp",EDGE,"E1.top"),sQuery(id+"F1.wireOp",EDGE,"E1.left"),sQuery(id+"F1.wireOp",EDGE,"E1.right"),sQuery(id+"F1.wireOp",EDGE,"E2.bottom"),sQuery(id+"F1.wireOp",EDGE,"E2.top"),sQuery(id+"F1.wireOp",EDGE,"E2.left"),sQuery(id+"F1.wireOp",EDGE,"E2.right"),sQuery(id+"F1.wireOp",EDGE,"E3.bottom"),sQuery(id+"F1.wireOp",EDGE,"E3.top"),sQuery(id+"F1.wireOp",EDGE,"E3.left"),sQuery(id+"F1.wireOp",EDGE,"E3.right"),sQuery(id+"F1.wireOp",EDGE,"E4.bottom"),sQuery(id+"F1.wireOp",EDGE,"E4.top"),sQuery(id+"F1.wireOp",EDGE,"E4.left"),sQuery(id+"F1.wireOp",EDGE,"E4.right"),sQuery(id+"F1.wireOp",EDGE,"E5.bottom"),sQuery(id+"F1.wireOp",EDGE,"E5.top"),sQuery(id+"F1.wireOp",EDGE,"E5.left"),sQuery(id+"F1.wireOp",EDGE,"E5.right"),sQuery(id+"F1.wireOp",EDGE,"E6.bottom"),sQuery(id+"F1.wireOp",EDGE,"E6.top"),sQuery(id+"F1.wireOp",EDGE,"E6.left"),sQuery(id+"F1.wireOp",EDGE,"E6.right")])]});
            var Q1;
            Q1=makeQuery(id+"F24.opExtrude","SWEPT_BODY",BODY,{"disambiguationData":[OSD([sQuery(id+"F23.wireOp",EDGE,"E35.MirrorCS"),sQuery(id+"F23.wireOp",EDGE,"E36.MirrorCS"),sQuery(id+"F23.wireOp",EDGE,"E37.MirrorCS"),sQuery(id+"F23.wireOp",EDGE,"E38.MirrorCS"),sQuery(id+"F23.wireOp",EDGE,"E39.MirrorCS"),sQuery(id+"F23.wireOp",EDGE,"E40.MirrorCS")])]});
            var Q2;
            Q2=makeQuery(id+"F24.opExtrude","SWEPT_BODY",BODY,{"disambiguationData":[OSD([sQuery(id+"F23.wireOp",EDGE,"E33.bottom"),sQuery(id+"F23.wireOp",EDGE,"E33.top"),sQuery(id+"F23.wireOp",EDGE,"E33.left"),sQuery(id+"F23.wireOp",EDGE,"E33.right"),sQuery(id+"F23.wireOp",EDGE,"E34.top"),sQuery(id+"F23.wireOp",EDGE,"E34.right")])]});
            booleanBodies(context, id + "F26", {"operationType" : BooleanOperationType.SUBTRACTION, "tools" : qUnion([Q0]), "targets" : qUnion([Q1, Q2]), "keepTools" : true});
        }
        {
            var Q0;
            Q0=makeQuery(id+"F24.opExtrude","SWEPT_FACE",FACE,{"disambiguationData":[OSD([sQuery(id+"F23.wireOp",EDGE,"E38.MirrorCS")])]});
            var sketch = newSketch(context, id + "F27", { "sketchPlane" : qUnion([Q0])});
            skLineSegment(sketch, "E41.bottom", {"start": v(-431.8, -253.75) * mm, "end": v(203.2, -253.75) * mm});
            skLineSegment(sketch, "E41.top", {"start": v(-431.8, -228.35) * mm, "end": v(203.2, -228.35) * mm});
            skLineSegment(sketch, "E41.left", {"start": v(-431.8, -253.75) * mm, "end": v(-431.8, -228.35) * mm});
            skLineSegment(sketch, "E41.right", {"start": v(203.2, -253.75) * mm, "end": v(203.2, -228.35) * mm});
            skSolve(sketch);
        }
        {
            var Q0;
            Q0 = qSketchRegion(id + "F27", true);
            extrude(context, id + "F28", {"entities" : qUnion([Q0]), "oppositeDirection" : true, "depth" : (getVariable(context, 'ply')) * mm, "offsetDistance" : 25.4 * mm});
        }
        {
            var Q0;
            Q0=makeQuery(id+"F11.opExtrude","SWEPT_FACE",FACE,{"disambiguationData":[OSD([sQuery(id+"F10.wireOp",EDGE,"E22.MirrorCS")])]});
            var sketch = newSketch(context, id + "F29", { "sketchPlane" : qUnion([Q0])});
            skLineSegment(sketch, "E42.bottom", {"start": v(-202.7, -228.6) * mm, "end": v(432.3, -228.6) * mm});
            skLineSegment(sketch, "E42.top", {"start": v(-202.7, -254) * mm, "end": v(432.3, -254) * mm});
            skLineSegment(sketch, "E42.left", {"start": v(-202.7, -228.6) * mm, "end": v(-202.7, -254) * mm});
            skLineSegment(sketch, "E42.right", {"start": v(432.3, -228.6) * mm, "end": v(432.3, -254) * mm});
            skSolve(sketch);
        }
        {
            var Q0;
            Q0 = qSketchRegion(id + "F29", true);
            extrude(context, id + "F30", {"entities" : qUnion([Q0]), "oppositeDirection" : true, "depth" : (getVariable(context, 'ply')) * mm, "offsetDistance" : 25.4 * mm});
        }
        {
            var Q0;
            Q0=makeQuery(id+"F28.opExtrude","SWEPT_BODY",BODY,{"disambiguationData":[OSD([sQuery(id+"F27.wireOp",EDGE,"E41.bottom"),sQuery(id+"F27.wireOp",EDGE,"E41.top"),sQuery(id+"F27.wireOp",EDGE,"E41.left"),sQuery(id+"F27.wireOp",EDGE,"E41.right")])]});
            var Q1;
            Q1=makeQuery(id+"F24.opExtrude","SWEPT_BODY",BODY,{"disambiguationData":[OSD([sQuery(id+"F23.wireOp",EDGE,"E35.MirrorCS"),sQuery(id+"F23.wireOp",EDGE,"E36.MirrorCS"),sQuery(id+"F23.wireOp",EDGE,"E37.MirrorCS"),sQuery(id+"F23.wireOp",EDGE,"E38.MirrorCS"),sQuery(id+"F23.wireOp",EDGE,"E39.MirrorCS"),sQuery(id+"F23.wireOp",EDGE,"E40.MirrorCS")])]});
            var Q2;
            Q2=makeQuery(id+"F18.opExtrude","SWEPT_BODY",BODY,{"disambiguationData":[OSD([sQuery(id+"F17.wireOp",EDGE,"E25.bottom"),sQuery(id+"F17.wireOp",EDGE,"E25.top"),sQuery(id+"F17.wireOp",EDGE,"E25.left"),sQuery(id+"F17.wireOp",EDGE,"E25.right"),sQuery(id+"F17.wireOp",EDGE,"E26.top"),sQuery(id+"F17.wireOp",EDGE,"E26.right")])]});
            var Q3;
            Q3=makeQuery(id+"F11.opExtrude","SWEPT_BODY",BODY,{"disambiguationData":[OSD([sQuery(id+"F10.wireOp",EDGE,"E17.bottom"),sQuery(id+"F10.wireOp",EDGE,"E17.top"),sQuery(id+"F10.wireOp",EDGE,"E17.left"),sQuery(id+"F10.wireOp",EDGE,"E17.right"),sQuery(id+"F10.wireOp",EDGE,"E18.top"),sQuery(id+"F10.wireOp",EDGE,"E18.right")])]});
            booleanBodies(context, id + "F31", {"operationType" : BooleanOperationType.SUBTRACTION, "tools" : qUnion([Q0]), "targets" : qUnion([Q1, Q2, Q3]), "keepTools" : true});
        }
        {
            var Q0;
            Q0=makeQuery(id+"F30.opExtrude","SWEPT_BODY",BODY,{"disambiguationData":[OSD([sQuery(id+"F29.wireOp",EDGE,"E42.bottom"),sQuery(id+"F29.wireOp",EDGE,"E42.top"),sQuery(id+"F29.wireOp",EDGE,"E42.left"),sQuery(id+"F29.wireOp",EDGE,"E42.right")])]});
            var Q1;
            Q1=makeQuery(id+"F11.opExtrude","SWEPT_BODY",BODY,{"disambiguationData":[OSD([sQuery(id+"F10.wireOp",EDGE,"E19.MirrorCS"),sQuery(id+"F10.wireOp",EDGE,"E20.MirrorCS"),sQuery(id+"F10.wireOp",EDGE,"E21.MirrorCS"),sQuery(id+"F10.wireOp",EDGE,"E22.MirrorCS"),sQuery(id+"F10.wireOp",EDGE,"E23.MirrorCS"),sQuery(id+"F10.wireOp",EDGE,"E24.MirrorCS")])]});
            var Q2;
            Q2=makeQuery(id+"F18.opExtrude","SWEPT_BODY",BODY,{"disambiguationData":[OSD([sQuery(id+"F17.wireOp",EDGE,"E27.MirrorCS"),sQuery(id+"F17.wireOp",EDGE,"E28.MirrorCS"),sQuery(id+"F17.wireOp",EDGE,"E29.MirrorCS"),sQuery(id+"F17.wireOp",EDGE,"E30.MirrorCS"),sQuery(id+"F17.wireOp",EDGE,"E31.MirrorCS"),sQuery(id+"F17.wireOp",EDGE,"E32.MirrorCS")])]});
            var Q3;
            Q3=makeQuery(id+"F24.opExtrude","SWEPT_BODY",BODY,{"disambiguationData":[OSD([sQuery(id+"F23.wireOp",EDGE,"E33.bottom"),sQuery(id+"F23.wireOp",EDGE,"E33.top"),sQuery(id+"F23.wireOp",EDGE,"E33.left"),sQuery(id+"F23.wireOp",EDGE,"E33.right"),sQuery(id+"F23.wireOp",EDGE,"E34.top"),sQuery(id+"F23.wireOp",EDGE,"E34.right")])]});
            booleanBodies(context, id + "F32", {"operationType" : BooleanOperationType.SUBTRACTION, "tools" : qUnion([Q0]), "targets" : qUnion([Q1, Q2, Q3]), "keepTools" : true});
        }
    });
